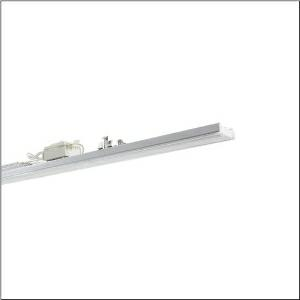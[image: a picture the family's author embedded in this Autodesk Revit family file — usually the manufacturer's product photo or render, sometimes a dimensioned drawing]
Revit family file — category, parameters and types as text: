
# Revit family: licross_r__11_recessed_mo_51te127n485g_69df
name_source: partatom
category: Lighting Fixtures
units: mm (PartAtom-declared; Revit-internal decimal feet)

## family parameters
Cut with Voids When Loaded = No
Host = Face
Light Source = No
Part Type = Normal
Room Calculation Point = No
Round Connector Dimension = Use Diameter
Shared = No

## types (1)
- Licross® 11 Recessed MO (1 x LED, 8950 lm, 48.5 W, 4000K)
    Apparent Load = 49 VA
    CIE Flux Codes = 67 92 99 100 100
    Color Rendering = 80
    Color Temperature = 4000K
    Default Elevation = 1800 mm
    Description = Licross® 11 Recessed MO, luminaire insert, of sheet steel, galvanised, coil coated, white, length: 1.500mm, width: 66mm, height: 67mm, LED rated luminous flux: 8.950lm, light colour: 840, control gear: ON/OFF, with plug, 3-pole, with phase selection, mains connection: 220..240V, AC, 50/60Hz, rated input power: 49W, internal wiring halogen-free, primary optical cover: cover, of PMMA, light emission: direct distribution, primary light characteristic: symmetric, protection rating (complete): IP54, insulation class (complete): insulation class I (protective earthing), certification: CE, ENEC, VDE, UKCA, protection symbol: D if used in an environment with non-conductive dust loads with corresponding accessories, impact resistance: IK06, permissible ambient temperature for indoor applications: -35..+35°C, corresponds to IFS (International Featured Standards) requirements for safety and quality in the food industry, reducing of maximum allowable ambient temperature of 5°C with ceiling mounting, packaging unit: 1 piece
    Height = 58 mm
    Lamp = 1 x LED
    Lamp Light Flux = 8950 lm
    Lamp Power = 48.5 W
    Lamp count = 1
    Length = 1500 mm
    Luminous efficacy = 185 lm/W
    Manufacturer = Siteco
    ModVariant = No
    Model = 51TE127N485G
    Mounting Place = Ceiling
    Mounting Type = Pendant
    Number of Poles = 1
    OnlyDefault = Yes
    Power Factor = 1
    Product Name = Licross® 11 Recessed MO
    Product group = luminaire insert | ceiling pendant
    ProductGroupID = 902
    Protection Class = Protection class I
    Protection Degree = IP 54
    RLX_Detail_Level = 1
    RLX_Emergency_Light_Flux = 0 lm
    RLX_Emergency_Type = 0
    RLX_Emergency_Type_DB = No
    RlxData = <blob elided: 20769 chars, md5=928533b6>
    Socket = socket
    Standby Power = 0 W
    System Light Flux = 8950 lm
    System Power = 49 W
    Type Comments = Product without accessories
    Type Image = l_1296930.jpg
    URL = http://relux.com
    VarID = ---
    Voltage = 0 V
    Weight = 0.00 kg
    Width = 66 mm

## geometry (parser evidence)
native form markers: Blend x4, Sweep x9
no freeform markers — native parametric forms only
